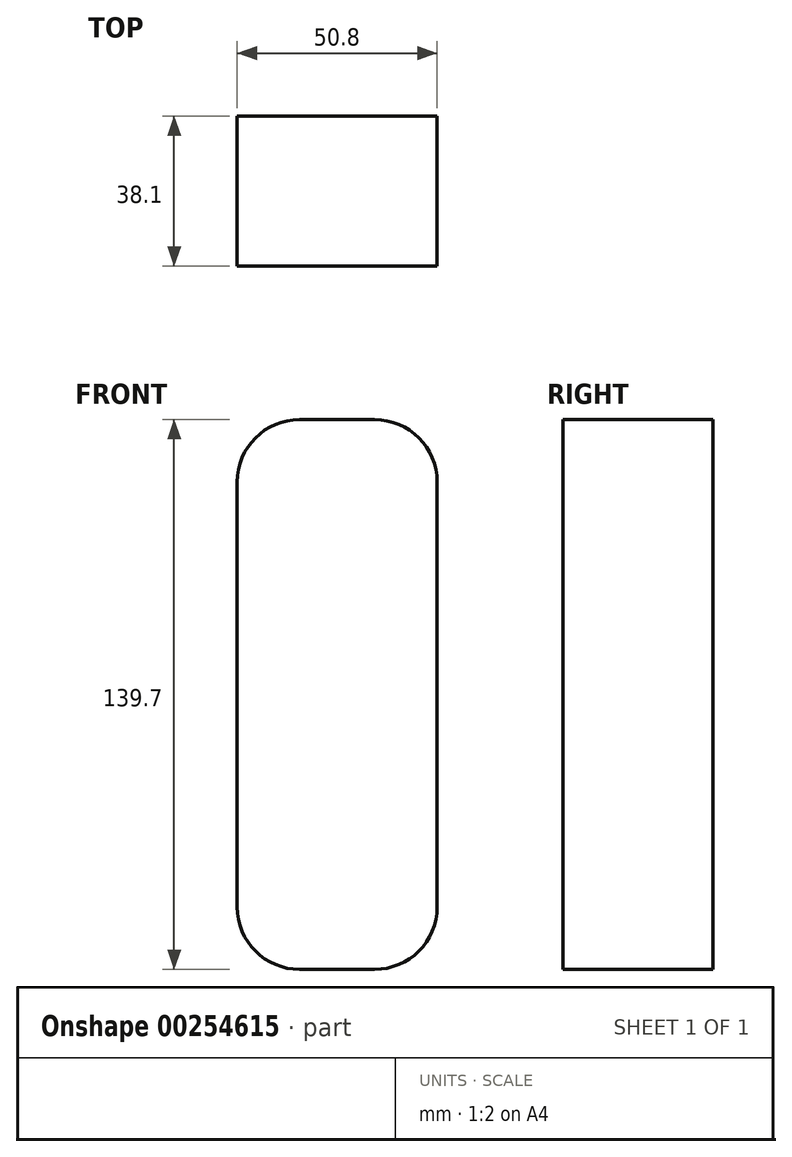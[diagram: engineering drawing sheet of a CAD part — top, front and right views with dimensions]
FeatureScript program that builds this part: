
annotation { "Feature Type Name" : "Feature", "Feature Type Description" : "" }
export const myFeature = defineFeature(function(context is Context, id is Id, definition is map)
    precondition{}
    {
        {
            var Q0;
            Q0=qCreatedBy(makeId("Front.planeOp"),FACE);
            var sketch = newSketch(context, id + "F0", { "sketchPlane" : qUnion([Q0])});
            skLineSegment(sketch, "E0.bottom", {"start": v(9.52, 69.85) * mm, "end": v(-9.53, 69.85) * mm});
            skLineSegment(sketch, "E0.top", {"start": v(9.52, -69.85) * mm, "end": v(-9.53, -69.85) * mm});
            skLineSegment(sketch, "E0.left", {"start": v(25.4, 53.98) * mm, "end": v(25.4, -53.98) * mm});
            skLineSegment(sketch, "E0.right", {"start": v(-25.4, 53.98) * mm, "end": v(-25.4, -53.98) * mm});
            skPoint(sketch, "E0.middle", {"position": v(0, 0) * mm});
            skPoint(sketch, "E1.visualSharp", {"position": v(-25.4, 69.85) * mm});
            skArc(sketch, "E1.filletArc", {"start": v(-9.53, 69.85) * mm, "mid": v(-20.75, 65.2) * mm, "end": v(-25.4, 53.98) * mm});
            skPoint(sketch, "E2.visualSharp", {"position": v(25.4, 69.85) * mm});
            skArc(sketch, "E2.filletArc", {"start": v(25.4, 53.98) * mm, "mid": v(20.75, 65.2) * mm, "end": v(9.52, 69.85) * mm});
            skPoint(sketch, "E3.visualSharp", {"position": v(25.4, -69.85) * mm});
            skArc(sketch, "E3.filletArc", {"start": v(9.52, -69.85) * mm, "mid": v(20.75, -65.2) * mm, "end": v(25.4, -53.98) * mm});
            skPoint(sketch, "E4.visualSharp", {"position": v(-25.4, -69.85) * mm});
            skArc(sketch, "E4.filletArc", {"start": v(-25.4, -53.98) * mm, "mid": v(-20.75, -65.2) * mm, "end": v(-9.53, -69.85) * mm});
            skSolve(sketch);
        }
        {
            var Q0;
            Q0=makeQuery(id+"F0.imprint","IMPRINT",FACE,{"disambiguationData":[TD([[makeQuery(id+"F0.imprint","IMPRINT",EDGE,{"derivedFrom":sQuery(id+"F0.wireOp",EDGE,"E0.bottom")}),1.0]])]});
            extrude(context, id + "F1", {"entities" : qUnion([Q0]), "depth" : 38.1 * mm});
        }
    });
